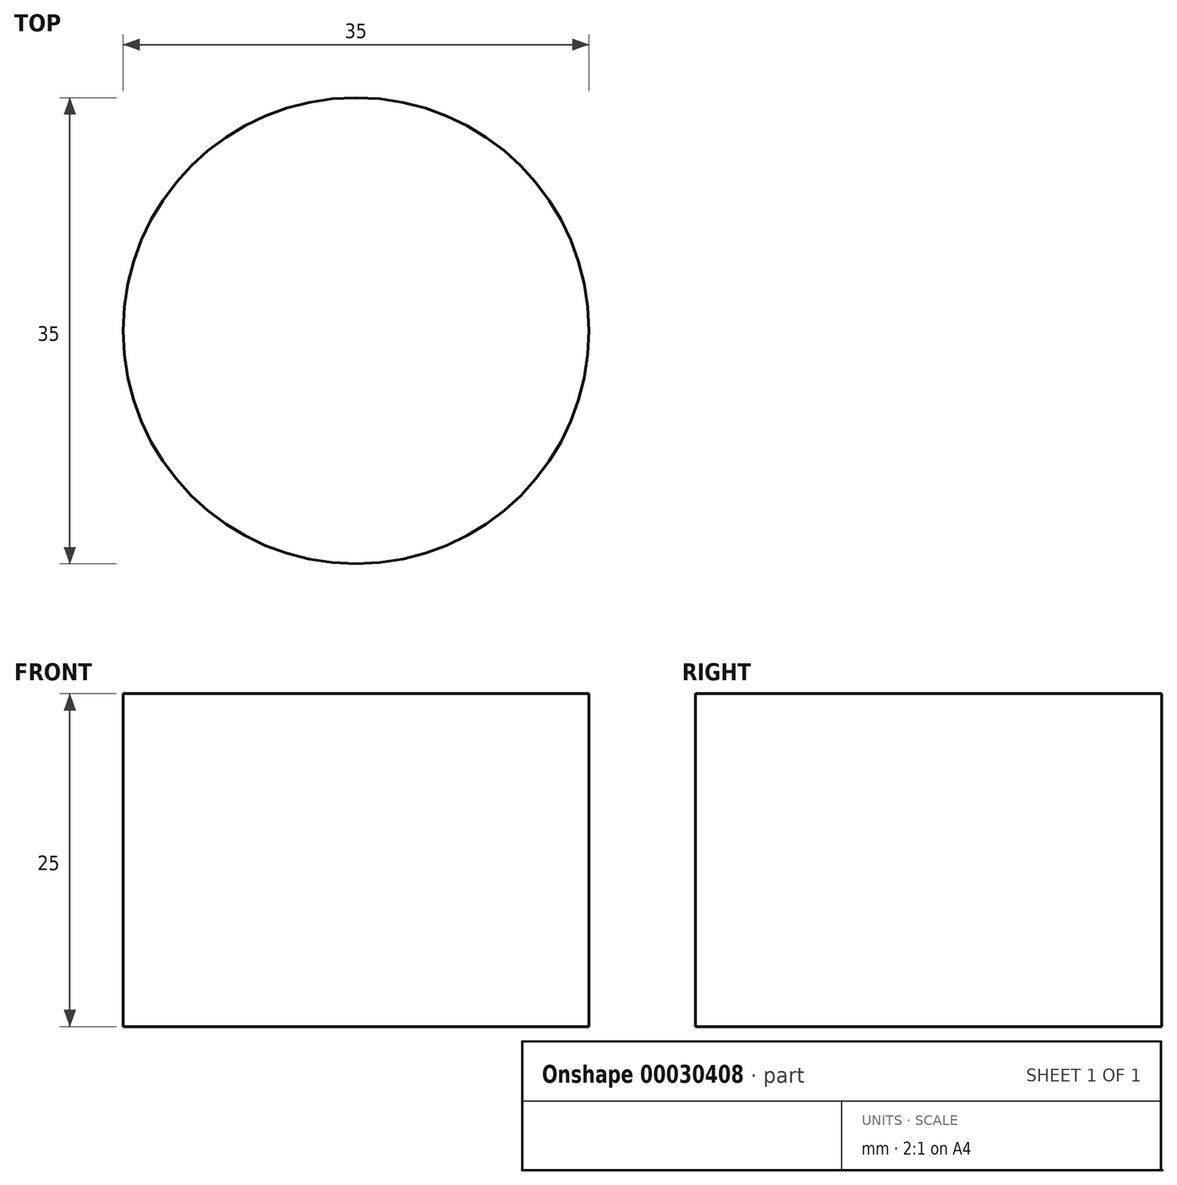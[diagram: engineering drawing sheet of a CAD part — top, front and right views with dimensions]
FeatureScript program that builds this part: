
annotation { "Feature Type Name" : "Feature", "Feature Type Description" : "" }
export const myFeature = defineFeature(function(context is Context, id is Id, definition is map)
    precondition{}
    {
        {
            var Q0;
            Q0=qCreatedBy(makeId("Top.planeOp"),FACE);
            var sketch = newSketch(context, id + "F0", { "sketchPlane" : qUnion([Q0])});
            skLineSegment(sketch, "E0.bottom", {"start": v(-75.61, -6.65) * mm, "end": v(79.39, -6.65) * mm});
            skLineSegment(sketch, "E0.top", {"start": v(-47.61, -31.65) * mm, "end": v(-37.61, -31.65) * mm});
            skLineSegment(sketch, "E0.left", {"start": v(-75.61, -6.65) * mm, "end": v(-75.61, -31.65) * mm});
            skLineSegment(sketch, "E1.top", {"start": v(-75.61, -61.68) * mm, "end": v(-65.61, -61.68) * mm});
            skLineSegment(sketch, "E1.left", {"start": v(-75.61, -31.68) * mm, "end": v(-75.61, -61.68) * mm});
            skLineSegment(sketch, "E1.right", {"start": v(-65.61, -31.68) * mm, "end": v(-65.61, -61.68) * mm});
            skLineSegment(sketch, "E2.top", {"start": v(-55.61, -46.65) * mm, "end": v(-47.61, -46.65) * mm});
            skLineSegment(sketch, "E2.left", {"start": v(-55.61, -31.65) * mm, "end": v(-55.61, -46.65) * mm});
            skLineSegment(sketch, "E2.right", {"start": v(-47.61, -31.65) * mm, "end": v(-47.61, -46.65) * mm});
            skLineSegment(sketch, "E3", {"start": v(-37.61, -31.65) * mm, "end": v(-30.61, -44.91) * mm});
            skLineSegment(sketch, "E4", {"start": v(-30.61, -44.91) * mm, "end": v(-23.61, -31.65) * mm});
            skArc(sketch, "E5", {"start": v(79.39, -31.65) * mm, "mid": v(147.08, -19.15) * mm, "end": v(79.39, -6.65) * mm});
            skCircle(sketch, "E6", {"center": v(112.08, -19.15) * mm, "radius": 17.5 * mm});
            skLineSegment(sketch, "E7", {"start": v(112.08, -19.15) * mm, "end": v(-75.61, -19.15) * mm, "construction": true});
            skLineSegment(sketch, "E8.trimOffspring", {"start": v(-23.61, -31.65) * mm, "end": v(79.39, -31.65) * mm});
            skSolve(sketch);
        }
        {
            var Q0;
            Q0 = qSketchRegion(id + "F0", true);
            extrude(context, id + "F1", {"entities" : qUnion([Q0]), "depth" : 25 * mm});
        }
    });
